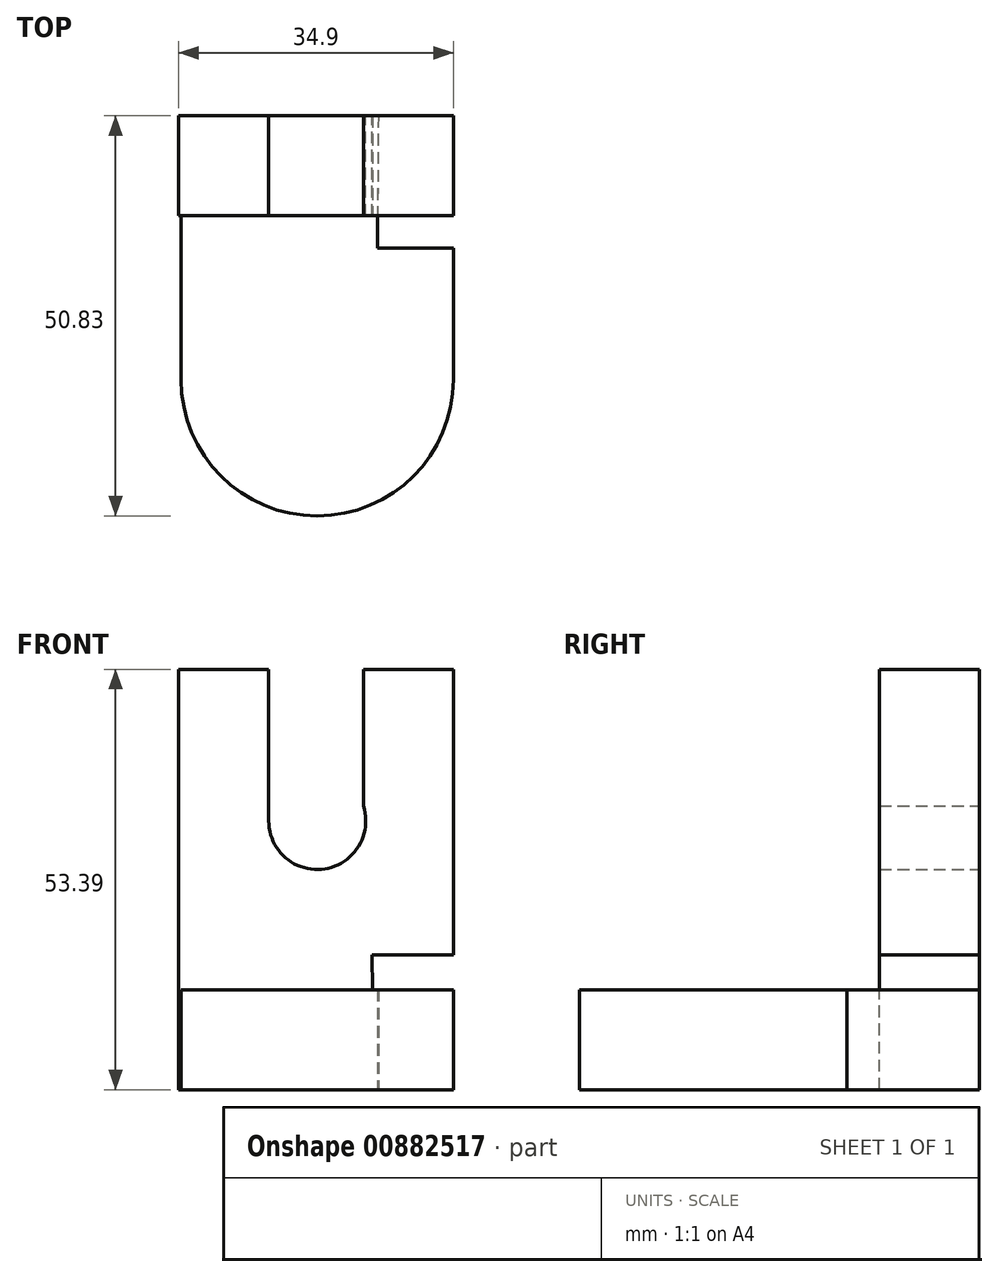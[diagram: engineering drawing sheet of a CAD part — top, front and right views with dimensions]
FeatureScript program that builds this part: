
annotation { "Feature Type Name" : "Feature", "Feature Type Description" : "" }
export const myFeature = defineFeature(function(context is Context, id is Id, definition is map)
    precondition{}
    {
        {
            var Q0;
            Q0=qCreatedBy(makeId("Top.planeOp"),FACE);
            var sketch = newSketch(context, id + "F0", { "sketchPlane" : qUnion([Q0])});
            skPoint(sketch, "E0.middle", {"position": v(0, -3.16) * mm});
            skPoint(sketch, "E1.bottom.start.orphan", {"position": v(17.3, 27.22) * mm});
            skPoint(sketch, "E0.right.end.orphan", {"position": v(-17.3, 27.22) * mm});
            skPoint(sketch, "E2.center.orphan", {"position": v(0, -33.54) * mm});
            skPoint(sketch, "E2.end.orphan", {"position": v(17.3, -33.54) * mm});
            skPoint(sketch, "E2.start.orphan", {"position": v(-17.3, -33.54) * mm});
            skLineSegment(sketch, "E3.bottom", {"start": v(-17.3, -33.54) * mm, "end": v(17.3, -33.54) * mm});
            skLineSegment(sketch, "E3.top", {"start": v(-17.3, 0) * mm, "end": v(7.76, 0) * mm});
            skLineSegment(sketch, "E3.left", {"start": v(-17.3, -33.54) * mm, "end": v(-17.3, 0) * mm});
            skLineSegment(sketch, "E3.right", {"start": v(17.3, -33.54) * mm, "end": v(17.3, -16.84) * mm});
            skArc(sketch, "E4", {"start": v(-17.3, -33.54) * mm, "mid": v(0, -50.83) * mm, "end": v(17.3, -33.54) * mm});
            skLineSegment(sketch, "E5.top", {"start": v(17.6, -16.84) * mm, "end": v(7.63, -16.84) * mm});
            skLineSegment(sketch, "E5.right", {"start": v(7.76, 0.15) * mm, "end": v(7.63, -16.84) * mm});
            skPoint(sketch, "E6.orphan", {"position": v(17.3, 0) * mm});
            skSolve(sketch);
        }
        {
            var Q0;
            Q0=qCreatedBy(makeId("Front.planeOp"),FACE);
            var sketch = newSketch(context, id + "F1", { "sketchPlane" : qUnion([Q0])});
            skPoint(sketch, "E7.middle", {"position": v(0, 0) * mm});
            skLineSegment(sketch, "E8.bottom", {"start": v(7.37, 0) * mm, "end": v(-17.6, 0) * mm});
            skLineSegment(sketch, "E8.top", {"start": v(17.3, 53.4) * mm, "end": v(5.87, 53.4) * mm});
            skLineSegment(sketch, "E8.left", {"start": v(17.3, 17.15) * mm, "end": v(17.3, 53.4) * mm});
            skLineSegment(sketch, "E8.right", {"start": v(-17.6, 0) * mm, "end": v(-17.6, 53.4) * mm});
            skLineSegment(sketch, "E9.left", {"start": v(-6.17, 34.14) * mm, "end": v(-6.17, 53.4) * mm});
            skLineSegment(sketch, "E9.right", {"start": v(5.87, 34.14) * mm, "end": v(5.87, 53.4) * mm});
            skPoint(sketch, "E9.middle", {"position": v(-0.15, 53.4) * mm});
            skArc(sketch, "E10", {"start": v(-6.17, 34.14) * mm, "mid": v(0.96, 28.05) * mm, "end": v(5.87, 36.04) * mm});
            skPoint(sketch, "E9.top.end.orphan", {"position": v(5.87, 72.64) * mm});
            skPoint(sketch, "E9.top.start.orphan", {"position": v(-6.17, 72.64) * mm});
            skLineSegment(sketch, "E11.trimOffspring", {"start": v(-6.17, 53.4) * mm, "end": v(-17.6, 53.4) * mm});
            skLineSegment(sketch, "E12.top", {"start": v(17.3, 17.15) * mm, "end": v(6.93, 17.15) * mm});
            skLineSegment(sketch, "E12.right", {"start": v(7.37, 0) * mm, "end": v(6.93, 17.15) * mm});
            skPoint(sketch, "E13.orphan", {"position": v(17.3, 0) * mm});
            skSolve(sketch);
        }
        {
            var Q0;
            Q0=makeQuery(id+"F0.imprint","IMPRINT",FACE,{"disambiguationData":[TD([[makeQuery(id+"F0.imprint","IMPRINT",EDGE,{"derivedFrom":sQuery(id+"F0.wireOp",EDGE,"E3.bottom")}),1.0]])]});
            var Q1;
            Q1=qSketchRegion(id+"F0",true);
            extrude(context, id + "F2", {"entities" : qUnion([Q0, Q1]), "depth" : 12.7 * mm, "offsetDistance" : 25.4 * mm});
        }
        {
            var Q0;
            Q0=makeQuery(id+"F1.imprint","IMPRINT",FACE,{"disambiguationData":[TD([[makeQuery(id+"F1.imprint","IMPRINT",EDGE,{"derivedFrom":sQuery(id+"F1.wireOp",EDGE,"E8.bottom")}),-1.0]])]});
            extrude(context, id + "F3", {"entities" : qUnion([Q0]), "operationType" : NewBodyOperationType.ADD, "depth" : 12.7 * mm, "offsetDistance" : 25.4 * mm});
        }
    });
